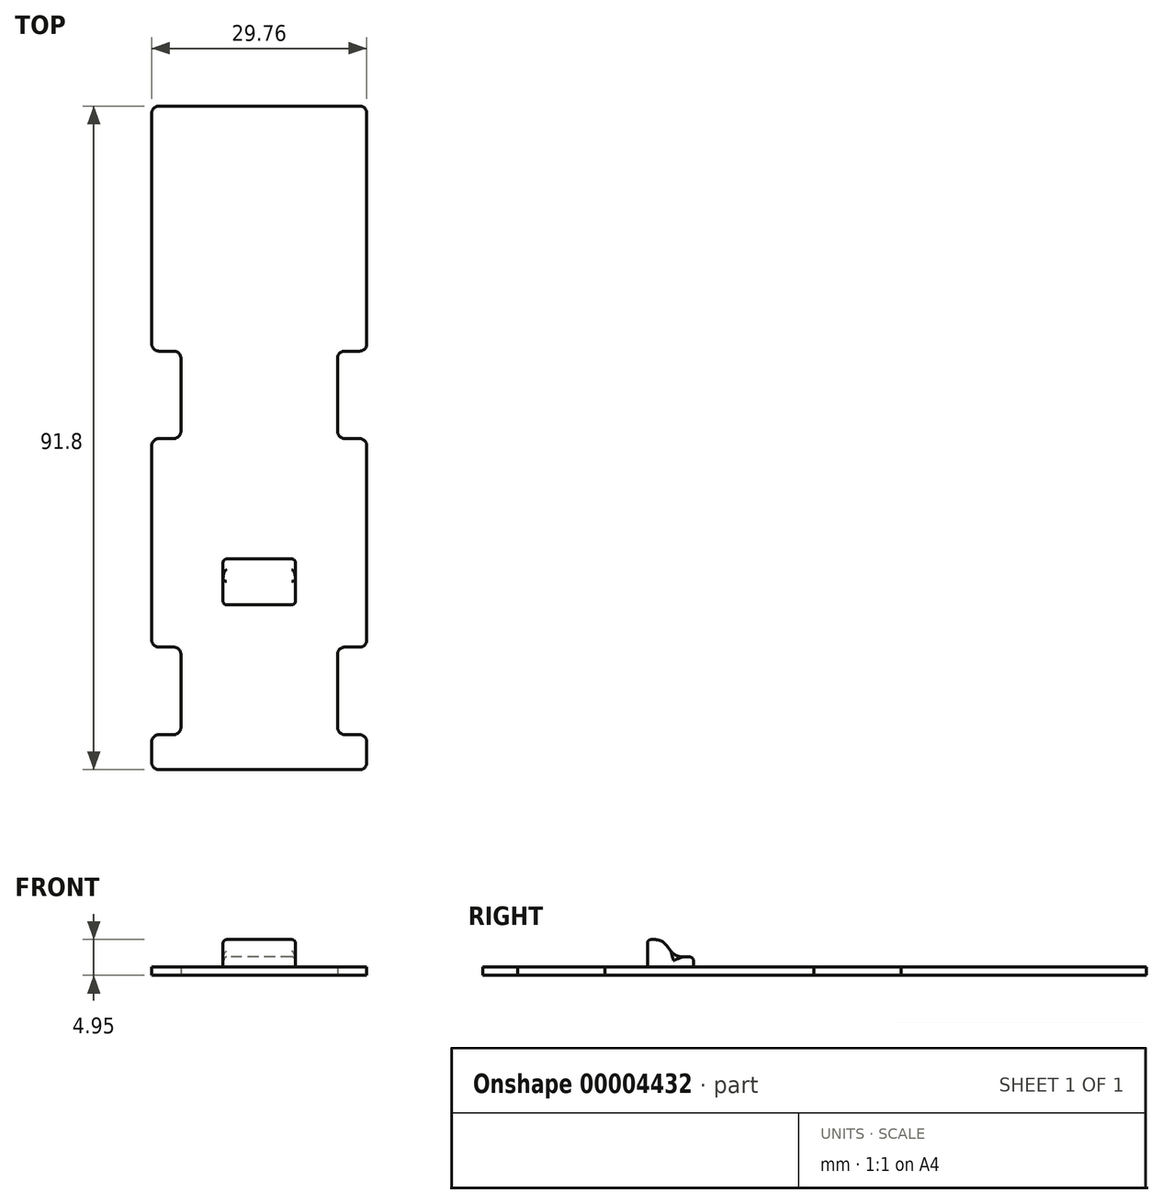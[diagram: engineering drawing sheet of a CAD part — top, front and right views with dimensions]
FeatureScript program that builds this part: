
annotation { "Feature Type Name" : "Feature", "Feature Type Description" : "" }
export const myFeature = defineFeature(function(context is Context, id is Id, definition is map)
    precondition{}
    {
        {
            var Q0;
            Q0=qCreatedBy(makeId("Top.planeOp"),FACE);
            var sketch = newSketch(context, id + "F0", { "sketchPlane" : qUnion([Q0])});
            skLineSegment(sketch, "E0", {"start": v(-14.88, 74.85) * mm, "end": v(-14.87, 40.95) * mm});
            skLineSegment(sketch, "E1", {"start": v(-14.88, 40.95) * mm, "end": v(-10.83, 40.95) * mm});
            skLineSegment(sketch, "E2", {"start": v(-10.83, 40.95) * mm, "end": v(-10.83, 28.85) * mm});
            skLineSegment(sketch, "E3", {"start": v(-10.83, 28.85) * mm, "end": v(-14.88, 28.85) * mm});
            skLineSegment(sketch, "E4", {"start": v(-14.88, 28.85) * mm, "end": v(-14.87, 0) * mm});
            skLineSegment(sketch, "E5", {"start": v(-14.88, 0) * mm, "end": v(-10.83, 0) * mm});
            skLineSegment(sketch, "E6", {"start": v(-10.83, 0) * mm, "end": v(-10.83, -12.1) * mm});
            skLineSegment(sketch, "E7", {"start": v(-10.83, -12.1) * mm, "end": v(-14.88, -12.1) * mm});
            skLineSegment(sketch, "E8", {"start": v(-14.88, -12.1) * mm, "end": v(-14.88, -16.95) * mm});
            skLineSegment(sketch, "E9", {"start": v(-14.88, -16.95) * mm, "end": v(14.88, -16.95) * mm});
            skLineSegment(sketch, "E10", {"start": v(14.88, -16.95) * mm, "end": v(14.88, -12.1) * mm});
            skLineSegment(sketch, "E11", {"start": v(14.88, -12.1) * mm, "end": v(10.83, -12.1) * mm});
            skLineSegment(sketch, "E12", {"start": v(10.82, -12.1) * mm, "end": v(10.82, 0) * mm});
            skLineSegment(sketch, "E13", {"start": v(10.83, 0) * mm, "end": v(14.88, 0) * mm});
            skLineSegment(sketch, "E14", {"start": v(14.88, 0) * mm, "end": v(14.88, 28.85) * mm});
            skLineSegment(sketch, "E15", {"start": v(14.88, 28.85) * mm, "end": v(10.83, 28.85) * mm});
            skLineSegment(sketch, "E16", {"start": v(10.82, 28.85) * mm, "end": v(10.82, 40.95) * mm});
            skLineSegment(sketch, "E17", {"start": v(10.83, 40.95) * mm, "end": v(14.88, 40.95) * mm});
            skLineSegment(sketch, "E18", {"start": v(14.88, 40.95) * mm, "end": v(14.88, 74.85) * mm});
            skLineSegment(sketch, "E19", {"start": v(14.88, 74.85) * mm, "end": v(-14.88, 74.85) * mm});
            skLineSegment(sketch, "E20", {"start": v(-10.83, 0) * mm, "end": v(10.83, 0) * mm, "construction": true});
            skSolve(sketch);
        }
        {
            var Q0;
            Q0=qSketchRegion(id+"F0",true);
            extrude(context, id + "F1", {"entities" : qUnion([Q0]), "depth" : 1.15 * mm});
        }
        {
            var Q0;
            Q0=makeQuery(id+"F1.opExtrude","SWEPT_EDGE",EDGE,{"disambiguationData":[OSD([sQuery(id+"F0.wireOp",EDGE,"E9"),sQuery(id+"F0.wireOp",EDGE,"E10")])]});
            var Q1;
            Q1=makeQuery(id+"F1.opExtrude","SWEPT_EDGE",EDGE,{"disambiguationData":[OSD([sQuery(id+"F0.wireOp",EDGE,"E10"),sQuery(id+"F0.wireOp",EDGE,"E11")])]});
            var Q2;
            Q2=makeQuery(id+"F1.opExtrude","SWEPT_EDGE",EDGE,{"disambiguationData":[OSD([sQuery(id+"F0.wireOp",EDGE,"E11"),sQuery(id+"F0.wireOp",EDGE,"E12")])]});
            var Q3;
            Q3=makeQuery(id+"F1.opExtrude","SWEPT_EDGE",EDGE,{"disambiguationData":[OSD([sQuery(id+"F0.wireOp",EDGE,"E12"),sQuery(id+"F0.wireOp",EDGE,"E13")])]});
            var Q4;
            Q4=makeQuery(id+"F1.opExtrude","SWEPT_EDGE",EDGE,{"disambiguationData":[OSD([sQuery(id+"F0.wireOp",EDGE,"E13"),sQuery(id+"F0.wireOp",EDGE,"E14")])]});
            var Q5;
            Q5=makeQuery(id+"F1.opExtrude","SWEPT_EDGE",EDGE,{"disambiguationData":[OSD([sQuery(id+"F0.wireOp",EDGE,"E14"),sQuery(id+"F0.wireOp",EDGE,"E15")])]});
            var Q6;
            Q6=makeQuery(id+"F1.opExtrude","SWEPT_EDGE",EDGE,{"disambiguationData":[OSD([sQuery(id+"F0.wireOp",EDGE,"E15"),sQuery(id+"F0.wireOp",EDGE,"E16")])]});
            var Q7;
            Q7=makeQuery(id+"F1.opExtrude","SWEPT_EDGE",EDGE,{"disambiguationData":[OSD([sQuery(id+"F0.wireOp",EDGE,"E16"),sQuery(id+"F0.wireOp",EDGE,"E17")])]});
            var Q8;
            Q8=makeQuery(id+"F1.opExtrude","SWEPT_EDGE",EDGE,{"disambiguationData":[OSD([sQuery(id+"F0.wireOp",EDGE,"E17"),sQuery(id+"F0.wireOp",EDGE,"E18")])]});
            var Q9;
            Q9=makeQuery(id+"F1.opExtrude","SWEPT_EDGE",EDGE,{"disambiguationData":[OSD([sQuery(id+"F0.wireOp",EDGE,"E18"),sQuery(id+"F0.wireOp",EDGE,"E19")])]});
            var Q10;
            Q10=makeQuery(id+"F1.opExtrude","SWEPT_EDGE",EDGE,{"disambiguationData":[OSD([sQuery(id+"F0.wireOp",EDGE,"E0"),sQuery(id+"F0.wireOp",EDGE,"E19")])]});
            var Q11;
            Q11=makeQuery(id+"F1.opExtrude","SWEPT_EDGE",EDGE,{"disambiguationData":[OSD([sQuery(id+"F0.wireOp",EDGE,"E0"),sQuery(id+"F0.wireOp",EDGE,"E1")])]});
            var Q12;
            Q12=makeQuery(id+"F1.opExtrude","SWEPT_EDGE",EDGE,{"disambiguationData":[OSD([sQuery(id+"F0.wireOp",EDGE,"E1"),sQuery(id+"F0.wireOp",EDGE,"E2")])]});
            var Q13;
            Q13=makeQuery(id+"F1.opExtrude","SWEPT_EDGE",EDGE,{"disambiguationData":[OSD([sQuery(id+"F0.wireOp",EDGE,"E2"),sQuery(id+"F0.wireOp",EDGE,"E3")])]});
            var Q14;
            Q14=makeQuery(id+"F1.opExtrude","SWEPT_EDGE",EDGE,{"disambiguationData":[OSD([sQuery(id+"F0.wireOp",EDGE,"E3"),sQuery(id+"F0.wireOp",EDGE,"E4")])]});
            var Q15;
            Q15=makeQuery(id+"F1.opExtrude","SWEPT_EDGE",EDGE,{"disambiguationData":[OSD([sQuery(id+"F0.wireOp",EDGE,"E4"),sQuery(id+"F0.wireOp",EDGE,"E5")])]});
            var Q16;
            Q16=makeQuery(id+"F1.opExtrude","SWEPT_EDGE",EDGE,{"disambiguationData":[OSD([sQuery(id+"F0.wireOp",EDGE,"E5"),sQuery(id+"F0.wireOp",EDGE,"E6")])]});
            var Q17;
            Q17=makeQuery(id+"F1.opExtrude","SWEPT_EDGE",EDGE,{"disambiguationData":[OSD([sQuery(id+"F0.wireOp",EDGE,"E7"),sQuery(id+"F0.wireOp",EDGE,"E8")])]});
            var Q18;
            Q18=makeQuery(id+"F1.opExtrude","SWEPT_EDGE",EDGE,{"disambiguationData":[OSD([sQuery(id+"F0.wireOp",EDGE,"E6"),sQuery(id+"F0.wireOp",EDGE,"E7")])]});
            var Q19;
            Q19=makeQuery(id+"F1.opExtrude","SWEPT_EDGE",EDGE,{"disambiguationData":[OSD([sQuery(id+"F0.wireOp",EDGE,"E8"),sQuery(id+"F0.wireOp",EDGE,"E9")])]});
            fillet(context, id + "F2", {"entities" : qUnion([Q0, Q1, Q2, Q3, Q4, Q5, Q6, Q7, Q8, Q9, Q10, Q11, Q12, Q13, Q14, Q15, Q16, Q17, Q18, Q19]), "radius" : 1 * mm, "tangentPropagation" : true, "allowEdgeOverflow" : false});
        }
        {
            var Q0;
            Q0=qCreatedBy(makeId("Right.planeOp"),FACE);
            var sketch = newSketch(context, id + "F3", { "sketchPlane" : qUnion([Q0])});
            skLineSegment(sketch, "E21", {"start": v(5.85, 1.15) * mm, "end": v(5.85, 4.95) * mm});
            skLineSegment(sketch, "E22", {"start": v(5.85, 4.95) * mm, "end": v(7.85, 4.95) * mm});
            skLineSegment(sketch, "E23", {"start": v(7.85, 4.95) * mm, "end": v(9.7, 2.55) * mm});
            skLineSegment(sketch, "E24", {"start": v(9.7, 2.55) * mm, "end": v(12.2, 2.55) * mm});
            skLineSegment(sketch, "E25", {"start": v(12.2, 2.55) * mm, "end": v(12.2, 1.15) * mm});
            skLineSegment(sketch, "E26", {"start": v(12.2, 1.15) * mm, "end": v(5.85, 1.15) * mm});
            skPoint(sketch, "E27", {"position": v(74.85, 1.15) * mm});
            skSolve(sketch);
        }
        {
            var Q0;
            Q0=qSketchRegion(id+"F3",true);
            extrude(context, id + "F4", {"entities" : qUnion([Q0]), "operationType" : NewBodyOperationType.ADD, "endBound" : BoundingType.SYMMETRIC, "depth" : 10 * mm});
        }
        {
            var Q0;
            Q0=makeQuery(id+"F4.opExtrude","CAP_EDGE",EDGE,{"disambiguationData":[OSD([sQuery(id+"F3.wireOp",EDGE,"E26")])],"isStart":false});
            var Q1;
            Q1=makeQuery(id+"F4.opExtrude","SWEPT_EDGE",EDGE,{"disambiguationData":[OSD([sQuery(id+"F3.wireOp",EDGE,"E21"),sQuery(id+"F3.wireOp",EDGE,"E26")])]});
            var Q2;
            Q2=makeQuery(id+"F4.opExtrude","CAP_EDGE",EDGE,{"disambiguationData":[OSD([sQuery(id+"F3.wireOp",EDGE,"E26")])],"isStart":true});
            var Q3;
            Q3=makeQuery(id+"F4.opExtrude","SWEPT_EDGE",EDGE,{"disambiguationData":[OSD([sQuery(id+"F3.wireOp",EDGE,"E25"),sQuery(id+"F3.wireOp",EDGE,"E26")])]});
            var Q4;
            Q4=makeQuery(id+"F4.opExtrude","SWEPT_EDGE",EDGE,{"disambiguationData":[OSD([sQuery(id+"F3.wireOp",EDGE,"E24"),sQuery(id+"F3.wireOp",EDGE,"E25")])]});
            var Q5;
            Q5=makeQuery(id+"F4.opExtrude","CAP_EDGE",EDGE,{"disambiguationData":[OSD([sQuery(id+"F3.wireOp",EDGE,"E24")])],"isStart":true});
            var Q6;
            Q6=makeQuery(id+"F4.opExtrude","CAP_EDGE",EDGE,{"disambiguationData":[OSD([sQuery(id+"F3.wireOp",EDGE,"E23")])],"isStart":true});
            var Q7;
            Q7=makeQuery(id+"F4.opExtrude","CAP_EDGE",EDGE,{"disambiguationData":[OSD([sQuery(id+"F3.wireOp",EDGE,"E22")])],"isStart":true});
            var Q8;
            Q8=makeQuery(id+"F4.opExtrude","SWEPT_EDGE",EDGE,{"disambiguationData":[OSD([sQuery(id+"F3.wireOp",EDGE,"E21"),sQuery(id+"F3.wireOp",EDGE,"E22")])]});
            var Q9;
            Q9=makeQuery(id+"F4.opExtrude","CAP_EDGE",EDGE,{"disambiguationData":[OSD([sQuery(id+"F3.wireOp",EDGE,"E21")])],"isStart":false});
            var Q10;
            Q10=makeQuery(id+"F4.opExtrude","CAP_EDGE",EDGE,{"disambiguationData":[OSD([sQuery(id+"F3.wireOp",EDGE,"E21")])],"isStart":true});
            var Q11;
            Q11=makeQuery(id+"F4.opExtrude","CAP_EDGE",EDGE,{"disambiguationData":[OSD([sQuery(id+"F3.wireOp",EDGE,"E22")])],"isStart":false});
            var Q12;
            Q12=makeQuery(id+"F4.opExtrude","CAP_EDGE",EDGE,{"disambiguationData":[OSD([sQuery(id+"F3.wireOp",EDGE,"E23")])],"isStart":false});
            var Q13;
            Q13=makeQuery(id+"F4.opExtrude","CAP_EDGE",EDGE,{"disambiguationData":[OSD([sQuery(id+"F3.wireOp",EDGE,"E24")])],"isStart":false});
            var Q14;
            Q14=makeQuery(id+"F4.opExtrude","CAP_EDGE",EDGE,{"disambiguationData":[OSD([sQuery(id+"F3.wireOp",EDGE,"E25")])],"isStart":false});
            var Q15;
            Q15=makeQuery(id+"F4.opExtrude","CAP_EDGE",EDGE,{"disambiguationData":[OSD([sQuery(id+"F3.wireOp",EDGE,"E25")])],"isStart":true});
            fillet(context, id + "F5", {"entities" : qUnion([Q0, Q1, Q2, Q3, Q4, Q5, Q6, Q7, Q8, Q9, Q10, Q11, Q12, Q13, Q14, Q15]), "radius" : 0.5 * mm, "tangentPropagation" : true, "allowEdgeOverflow" : false});
        }
        {
            var Q0;
            Q0=makeQuery(id+"F4.opExtrude","SWEPT_EDGE",EDGE,{"disambiguationData":[OSD([sQuery(id+"F3.wireOp",EDGE,"E22"),sQuery(id+"F3.wireOp",EDGE,"E23")])]});
            var Q1;
            Q1=makeQuery(id+"F4.opExtrude","SWEPT_EDGE",EDGE,{"disambiguationData":[OSD([sQuery(id+"F3.wireOp",EDGE,"E23"),sQuery(id+"F3.wireOp",EDGE,"E24")])]});
            fillet(context, id + "F6", {"entities" : qUnion([Q0, Q1]), "radius" : 2 * mm, "tangentPropagation" : true, "allowEdgeOverflow" : false});
        }
    });
